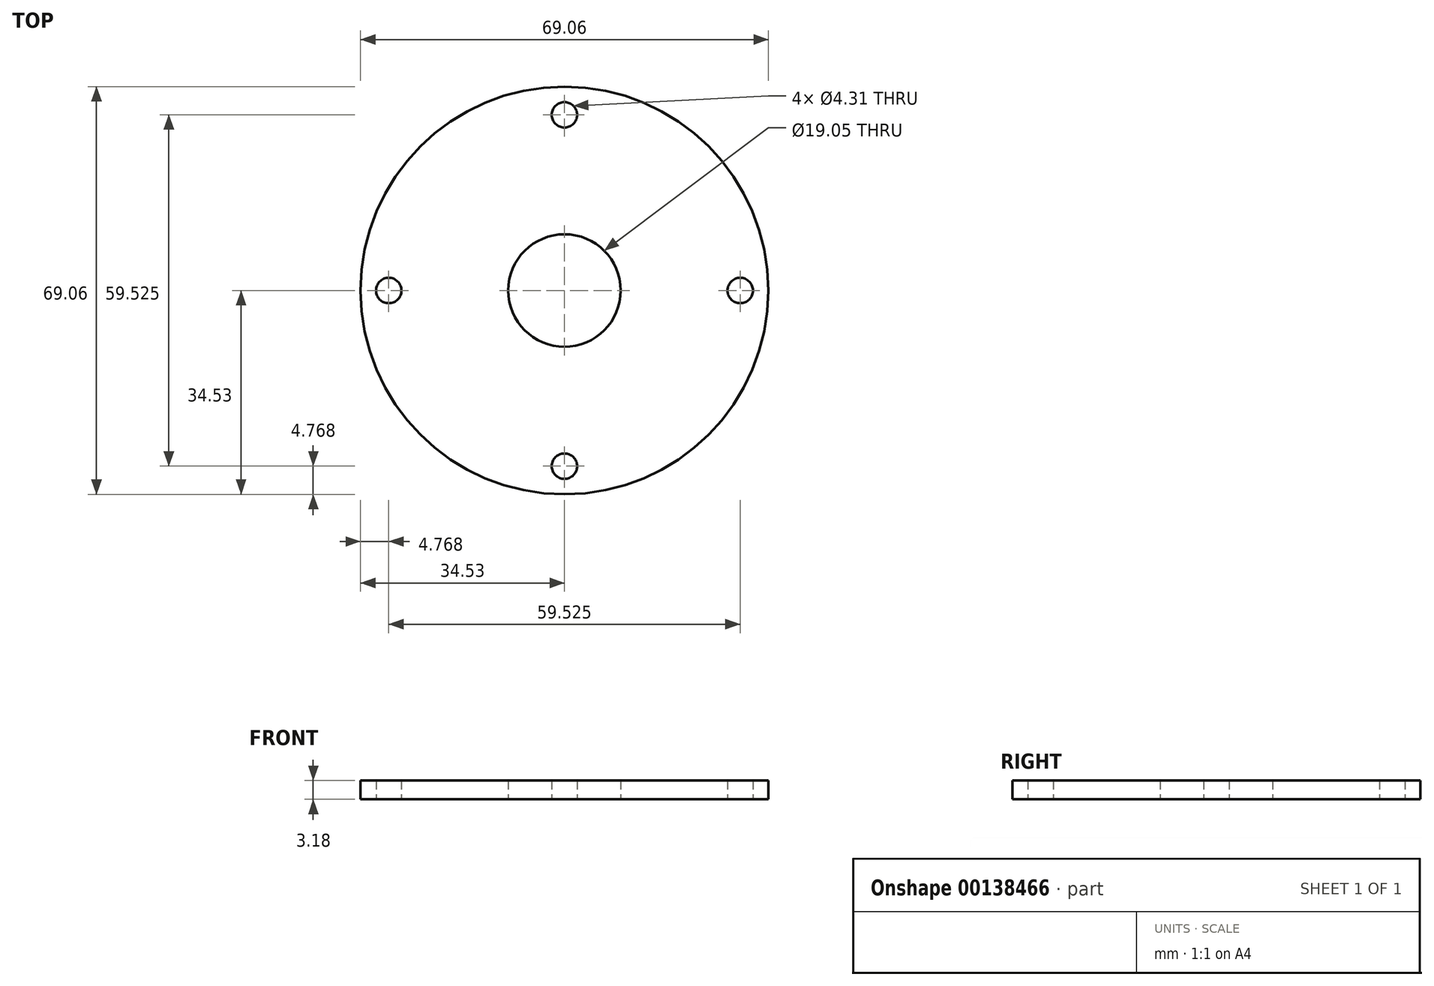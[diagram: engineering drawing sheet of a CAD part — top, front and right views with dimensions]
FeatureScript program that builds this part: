
annotation { "Feature Type Name" : "Feature", "Feature Type Description" : "" }
export const myFeature = defineFeature(function(context is Context, id is Id, definition is map)
    precondition{}
    {
        {
            var Q0;
            Q0=qCreatedBy(makeId("Top.planeOp"),FACE);
            var sketch = newSketch(context, id + "F0", { "sketchPlane" : qUnion([Q0])});
            skCircle(sketch, "E0", {"center": v(0, 0) * mm, "radius": 9.53 * mm});
            skCircle(sketch, "E1", {"center": v(0, 0) * mm, "radius": 34.53 * mm});
            skLineSegment(sketch, "E2", {"start": v(0, 29.76) * mm, "end": v(0, -29.76) * mm, "construction": true});
            skLineSegment(sketch, "E3", {"start": v(-29.76, 0) * mm, "end": v(29.76, 0) * mm, "construction": true});
            skCircle(sketch, "E4", {"center": v(0, 29.76) * mm, "radius": 4.76 * mm, "construction": true});
            skCircle(sketch, "E5", {"center": v(0, 29.76) * mm, "radius": 2.15 * mm});
            skCircle(sketch, "E6", {"center": v(29.76, 0) * mm, "radius": 2.15 * mm});
            skCircle(sketch, "E7", {"center": v(-29.76, 0) * mm, "radius": 2.15 * mm});
            skCircle(sketch, "E8", {"center": v(0, -29.76) * mm, "radius": 2.15 * mm});
            skSolve(sketch);
        }
        {
            var Q0;
            Q0 = qSketchRegion(id + "F0", true);
            extrude(context, id + "F1", {"entities" : qUnion([Q0]), "depth" : 3.17 * mm});
        }
    });
